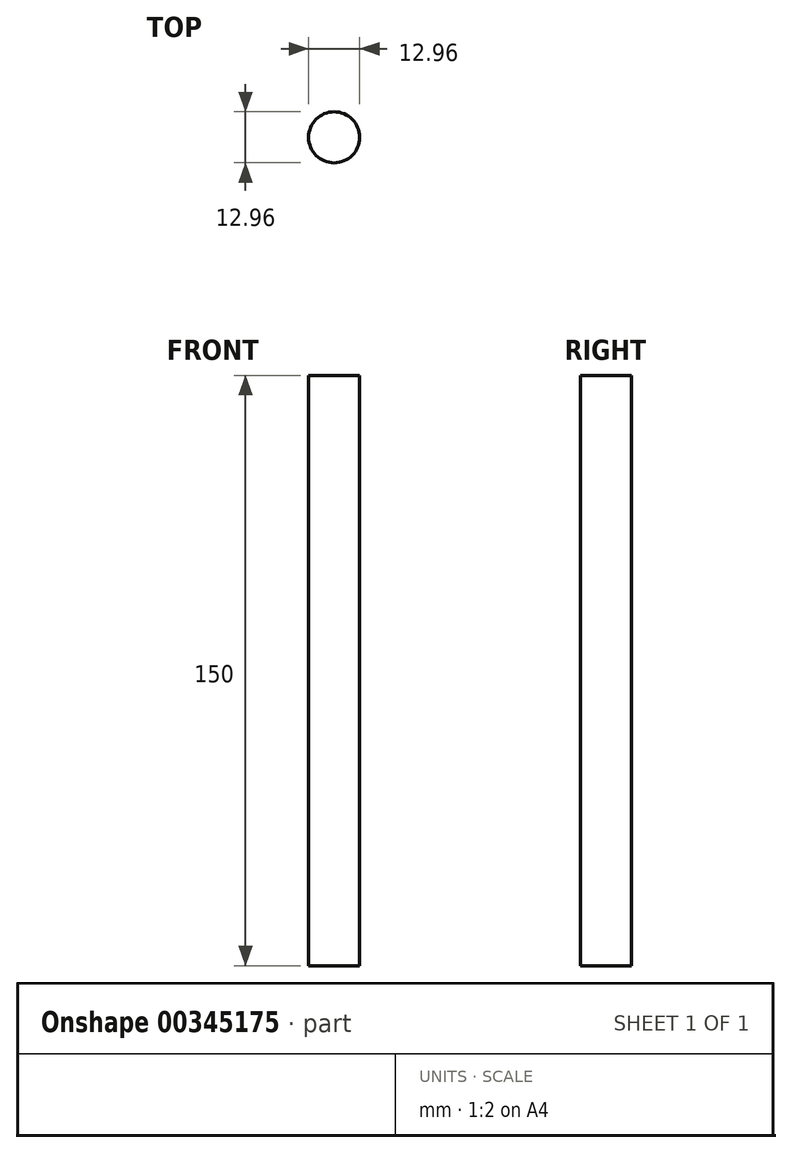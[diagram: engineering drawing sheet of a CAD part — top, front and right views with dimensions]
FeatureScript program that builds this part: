
annotation { "Feature Type Name" : "Feature", "Feature Type Description" : "" }
export const myFeature = defineFeature(function(context is Context, id is Id, definition is map)
    precondition{}
    {
        {
            var Q0;
            Q0=qCreatedBy(makeId("Top.planeOp"),FACE);
            var sketch = newSketch(context, id + "F0", { "sketchPlane" : qUnion([Q0])});
            skCircle(sketch, "E0", {"center": v(0, 0) * mm, "radius": 6.48 * mm});
            skSolve(sketch);
        }
        {
            var Q0;
            Q0=makeQuery(id+"F0.imprint","IMPRINT",FACE,{"disambiguationData":[TD([[makeQuery(id+"F0.imprint","IMPRINT",EDGE,{"derivedFrom":sQuery(id+"F0.wireOp",EDGE,"E0")}),1.0]])]});
            extrude(context, id + "F1", {"entities" : qUnion([Q0]), "depth" : 150 * mm});
        }
    });
